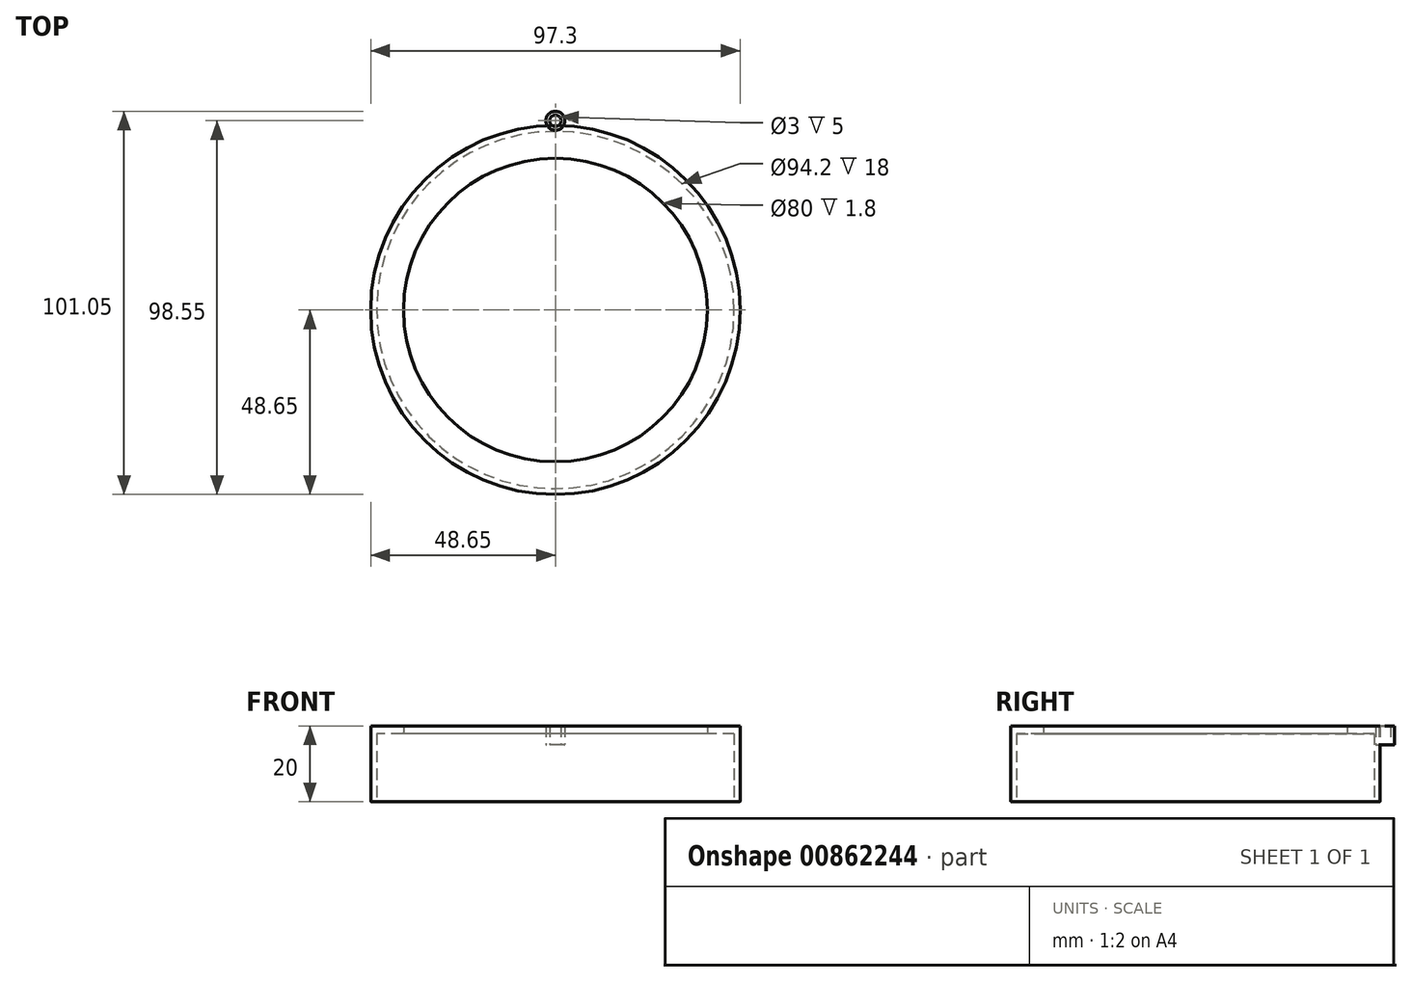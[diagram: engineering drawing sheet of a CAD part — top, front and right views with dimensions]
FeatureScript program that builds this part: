
annotation { "Feature Type Name" : "Feature", "Feature Type Description" : "" }
export const myFeature = defineFeature(function(context is Context, id is Id, definition is map)
    precondition{}
    {
        {
            var Q0;
            Q0=qCreatedBy(makeId("Top.planeOp"),FACE);
            var sketch = newSketch(context, id + "F0", { "sketchPlane" : qUnion([Q0])});
            skCircle(sketch, "E0", {"center": v(0, 0) * mm, "radius": 48.65 * mm});
            skSolve(sketch);
        }
        {
            var Q0;
            Q0 = qSketchRegion(id + "F0", true);
            extrude(context, id + "F1", {"entities" : qUnion([Q0]), "depth" : 20 * mm, "offsetDistance" : 25 * mm});
        }
        {
            var Q0;
            Q0=qCreatedBy(makeId("Top.planeOp"),FACE);
            var sketch = newSketch(context, id + "F2", { "sketchPlane" : qUnion([Q0])});
            skCircle(sketch, "E1", {"center": v(0, 0) * mm, "radius": 47.1 * mm});
            skSolve(sketch);
        }
        {
            var Q0;
            Q0 = qSketchRegion(id + "F2", true);
            extrude(context, id + "F3", {"entities" : qUnion([Q0]), "operationType" : NewBodyOperationType.REMOVE, "depth" : 18 * mm, "offsetDistance" : 25 * mm});
        }
        {
            var Q0;
            Q0=qCreatedBy(makeId("Top.planeOp"),FACE);
            var sketch = newSketch(context, id + "F4", { "sketchPlane" : qUnion([Q0])});
            skCircle(sketch, "E2", {"center": v(0, 0) * mm, "radius": 40 * mm});
            skSolve(sketch);
        }
        {
            var Q0;
            Q0 = qSketchRegion(id + "F4", true);
            extrude(context, id + "F5", {"entities" : qUnion([Q0]), "operationType" : NewBodyOperationType.REMOVE, "depth" : 20 * mm, "offsetDistance" : 25 * mm});
        }
        {
            var Q0;
            Q0=qCreatedBy(makeId("Top.planeOp"),FACE);
            var sketch = newSketch(context, id + "F6", { "sketchPlane" : qUnion([Q0])});
            skCircle(sketch, "E3", {"center": v(0, 0) * mm, "radius": 2.5 * mm});
            skSolve(sketch);
        }
        {
            var Q0;
            Q0 = qSketchRegion(id + "F6", true);
            extrude(context, id + "F7", {"entities" : qUnion([Q0]), "depth" : 5 * mm, "offsetDistance" : 25 * mm});
        }
        {
            var Q0;
            Q0=qCreatedBy(makeId("Top.planeOp"),FACE);
            var sketch = newSketch(context, id + "F8", { "sketchPlane" : qUnion([Q0])});
            skCircle(sketch, "E4", {"center": v(0, 0) * mm, "radius": 1.5 * mm});
            skSolve(sketch);
        }
        {
            var Q0;
            Q0 = qSketchRegion(id + "F8", true);
            extrude(context, id + "F9", {"entities" : qUnion([Q0]), "operationType" : NewBodyOperationType.REMOVE, "depth" : 5 * mm, "offsetDistance" : 25 * mm});
        }
        {
            var Q0;
            Q0=makeQuery(id+"F7.opExtrude","SWEPT_BODY",BODY,{"disambiguationData":[OSD([sQuery(id+"F6.wireOp",EDGE,"E3")])]});
            transform(context, id + "F10", {"entities" : qUnion([Q0]), "transformType" : TransformType.TRANSLATION_3D, "dx" : 0 * mm, "dy" : 49.3 * mm, "dz" : 15 * mm, "makeCopy" : false});
        }
        {
            var Q0;
            Q0=makeQuery(id+"F9.boolean.opBoolean","COPY",EDGE,{"derivedFrom":makeQuery(id+"F9.opExtrude","CAP_EDGE",EDGE,{"disambiguationData":[OSD([sQuery(id+"F8.wireOp",EDGE,"E4")])],"isStart":true})});
            var Q1;
            {var subQ0=sQuery(id+"F6.wireOp",EDGE,"E3");Q1=makeQuery(id+"FSxpGmv3hMyUSJF_2.opBoolean","SPLIT",EDGE,{"disambiguationData":[TD([makeQuery(id+"F1.opExtrude","SWEPT_FACE",FACE,{"disambiguationData":[OSD([sQuery(id+"F0.wireOp",EDGE,"E0")])]})])],"derivedFrom":makeQuery(id+"F7.opExtrude","CAP_EDGE",EDGE,{"disambiguationData":[OSD([subQ0])],"isStart":true})});}
            var Q2;
            Q2=makeQuery(id+"F1.opExtrude","CAP_EDGE",EDGE,{"disambiguationData":[OSD([sQuery(id+"F0.wireOp",EDGE,"E0")])],"isStart":true});
            var Q3;
            Q3=makeQuery(id+"F3.boolean.opBoolean","COPY",EDGE,{"derivedFrom":makeQuery(id+"F3.opExtrude","CAP_EDGE",EDGE,{"disambiguationData":[OSD([sQuery(id+"F2.wireOp",EDGE,"E1")])],"isStart":true})});
            var Q4;
            Q4=makeQuery(id+"F5.boolean.opBoolean","INTERSECT",EDGE,{"derivedFrom":[makeQuery(id+"F3.boolean.opBoolean","COPY",FACE,{"derivedFrom":makeQuery(id+"F3.opExtrude","CAP_FACE",FACE,{"disambiguationData":[OSD([sQuery(id+"F2.wireOp",EDGE,"E1")])],"isStart":false})}),makeQuery(id+"F5.opExtrude","SWEPT_FACE",FACE,{"disambiguationData":[OSD([sQuery(id+"F4.wireOp",EDGE,"E2")])]})]});
            fillet(context, id + "F11", {"entities" : qUnion([Q0, Q1, Q2, Q3, Q4]), "radius" : 0.2 * mm, "tangentPropagation" : true, "allowEdgeOverflow" : false});
        }
        {
            var Q0;
            Q0=makeQuery(id+"F7.opExtrude","SWEPT_BODY",BODY,{"disambiguationData":[OSD([sQuery(id+"F6.wireOp",EDGE,"E3")])]});
            transform(context, id + "F12", {"entities" : qUnion([Q0]), "transformType" : TransformType.TRANSLATION_3D, "dx" : 0 * mm, "dy" : 0.6 * mm, "dz" : 0 * mm, "makeCopy" : false});
        }
    });
